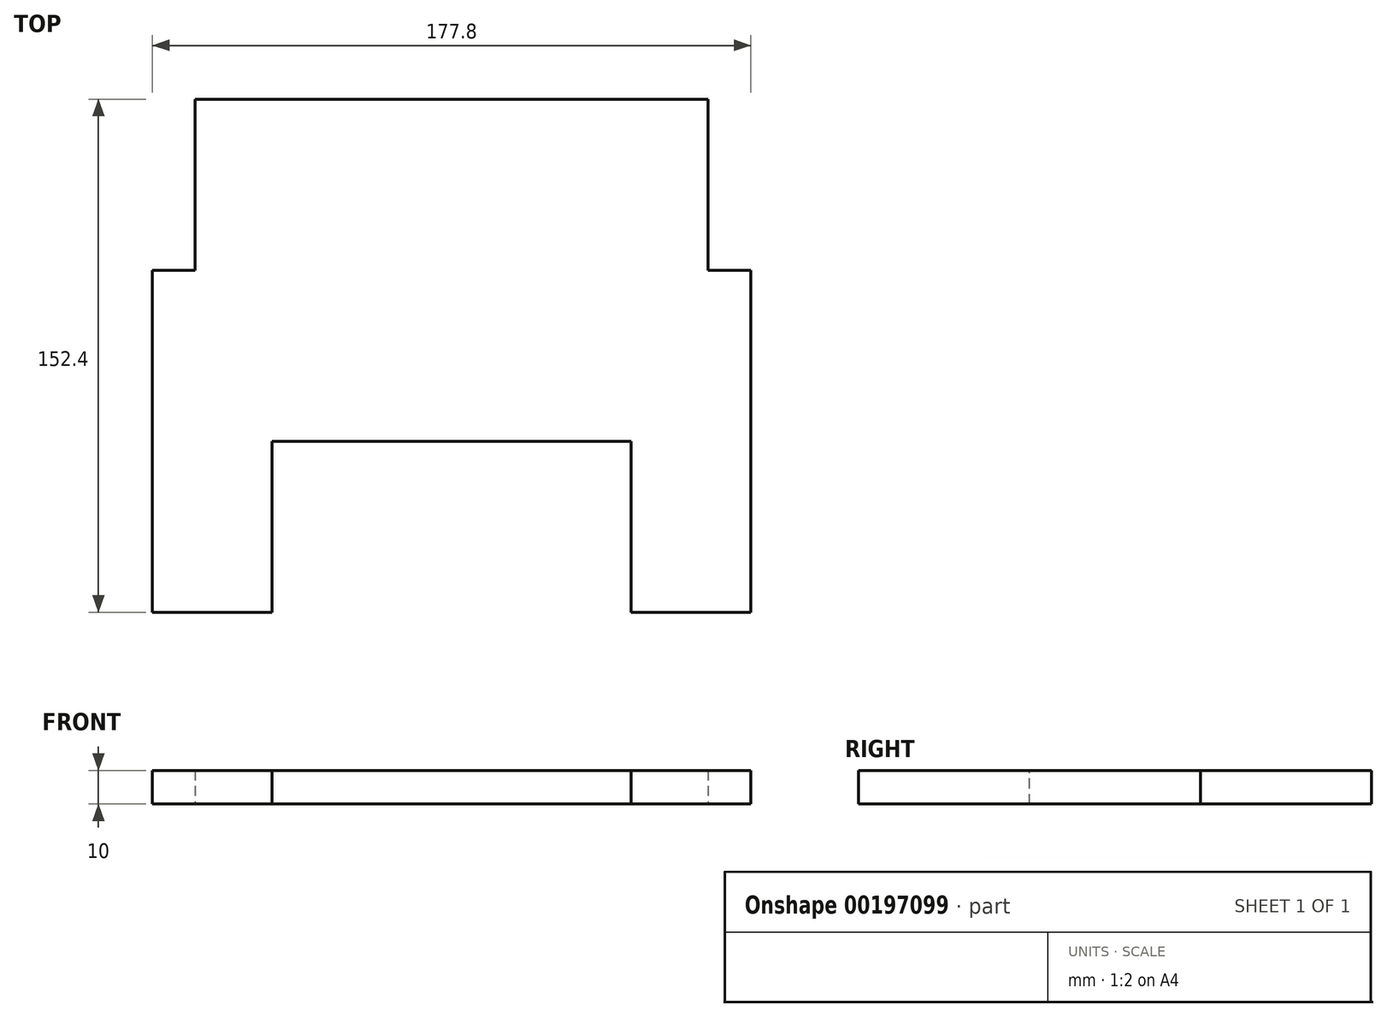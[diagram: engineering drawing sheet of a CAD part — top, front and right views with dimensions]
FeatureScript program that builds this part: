
annotation { "Feature Type Name" : "Feature", "Feature Type Description" : "" }
export const myFeature = defineFeature(function(context is Context, id is Id, definition is map)
    precondition{}
    {
        {
            var Q0;
            Q0=qCreatedBy(makeId("Top.planeOp"),FACE);
            var sketch = newSketch(context, id + "F0", { "sketchPlane" : qUnion([Q0])});
            skLineSegment(sketch, "E0.bottom", {"start": v(88.9, 25.4) * mm, "end": v(-88.9, 25.4) * mm});
            skLineSegment(sketch, "E0.top", {"start": v(88.9, -76.2) * mm, "end": v(-88.9, -76.2) * mm});
            skLineSegment(sketch, "E0.left", {"start": v(88.9, 25.4) * mm, "end": v(88.9, -76.2) * mm});
            skLineSegment(sketch, "E0.right", {"start": v(-88.9, 25.4) * mm, "end": v(-88.9, -76.2) * mm});
            skPoint(sketch, "E0.middle", {"position": v(0, 0) * mm});
            skLineSegment(sketch, "E1.bottom", {"start": v(-76.2, 0) * mm, "end": v(76.2, 0) * mm});
            skLineSegment(sketch, "E1.top", {"start": v(-76.2, 76.2) * mm, "end": v(76.2, 76.2) * mm});
            skLineSegment(sketch, "E1.left", {"start": v(-76.2, 0) * mm, "end": v(-76.2, 76.2) * mm});
            skLineSegment(sketch, "E1.right", {"start": v(76.2, 0) * mm, "end": v(76.2, 76.2) * mm});
            skSolve(sketch);
        }
        {
            var Q0;
            Q0 = qSketchRegion(id + "F0", true);
            extrude(context, id + "F1", {"entities" : qUnion([Q0]), "depth" : 10 * mm});
        }
        {
            var Q0;
            Q0=makeQuery(id+"F1.opExtrude","CAP_FACE",FACE,{"disambiguationData":[OSD([sQuery(id+"F0.wireOp",EDGE,"E0.bottom"),sQuery(id+"F0.wireOp",EDGE,"E0.top"),sQuery(id+"F0.wireOp",EDGE,"E0.left"),sQuery(id+"F0.wireOp",EDGE,"E0.right"),sQuery(id+"F0.wireOp",EDGE,"E1.top"),sQuery(id+"F0.wireOp",EDGE,"E1.left"),sQuery(id+"F0.wireOp",EDGE,"E1.right")])],"isStart":false});
            var sketch = newSketch(context, id + "F2", { "sketchPlane" : qUnion([Q0])});
            skLineSegment(sketch, "E2.bottom", {"start": v(-53.34, -76.2) * mm, "end": v(53.34, -76.2) * mm});
            skLineSegment(sketch, "E2.top", {"start": v(-53.34, -25.4) * mm, "end": v(53.34, -25.4) * mm});
            skLineSegment(sketch, "E2.left", {"start": v(-53.34, -76.2) * mm, "end": v(-53.34, -25.4) * mm});
            skLineSegment(sketch, "E2.right", {"start": v(53.34, -76.2) * mm, "end": v(53.34, -25.4) * mm});
            skSolve(sketch);
        }
        {
            var Q0;
            Q0 = qSketchRegion(id + "F2", true);
            extrude(context, id + "F3", {"entities" : qUnion([Q0]), "operationType" : NewBodyOperationType.REMOVE, "oppositeDirection" : true, "depth" : 25.4 * mm});
        }
    });
